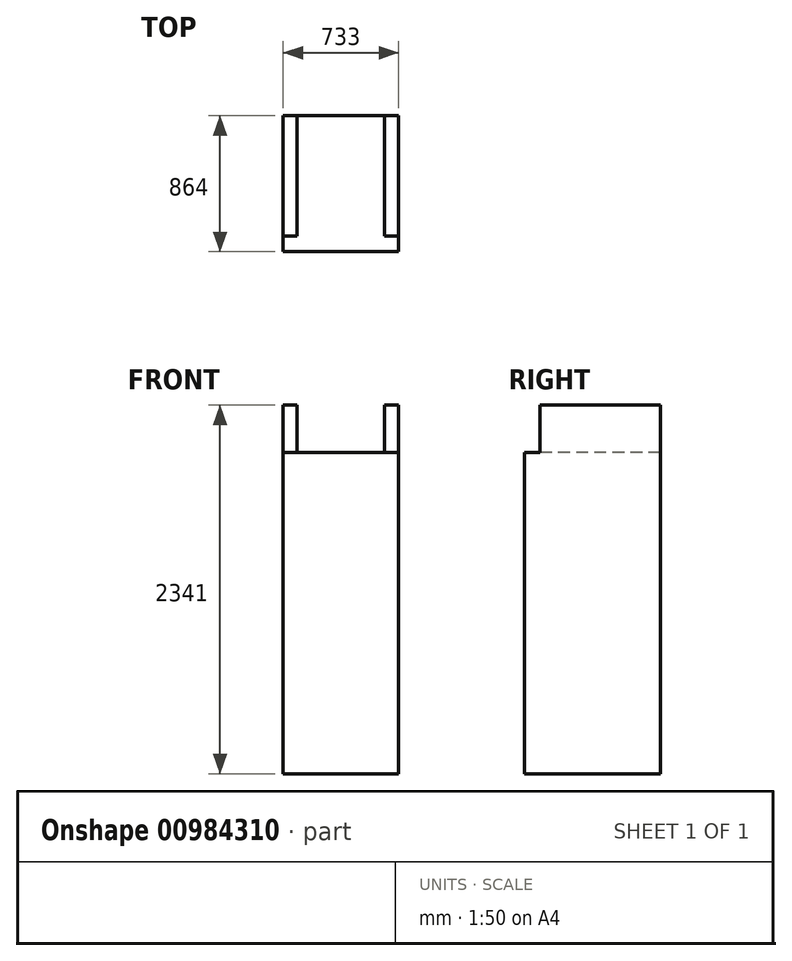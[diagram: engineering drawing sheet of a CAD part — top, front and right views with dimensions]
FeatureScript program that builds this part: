
annotation { "Feature Type Name" : "Feature", "Feature Type Description" : "" }
export const myFeature = defineFeature(function(context is Context, id is Id, definition is map)
    precondition{}
    {
        {
            var Q0;
            Q0=qCreatedBy(makeId("Top.planeOp"),FACE);
            var sketch = newSketch(context, id + "F0", { "sketchPlane" : qUnion([Q0])});
            skLineSegment(sketch, "E0.bottom", {"start": v(-733, 0) * mm, "end": v(0, 0) * mm});
            skLineSegment(sketch, "E0.top", {"start": v(-733, -764) * mm, "end": v(0, -764) * mm});
            skLineSegment(sketch, "E0.left", {"start": v(-733, 0) * mm, "end": v(-733, -764) * mm});
            skLineSegment(sketch, "E0.right", {"start": v(0, 0) * mm, "end": v(0, -764) * mm});
            skSolve(sketch);
        }
        {
            var Q0;
            Q0=makeQuery(id+"F0.imprint","IMPRINT",FACE,{"disambiguationData":[TD([[makeQuery(id+"F0.imprint","IMPRINT",EDGE,{"derivedFrom":sQuery(id+"F0.wireOp",EDGE,"E0.bottom")}),-1.0]])]});
            extrude(context, id + "F1", {"entities" : qUnion([Q0]), "depth" : 2341 * mm, "offsetDistance" : 25 * mm});
        }
        {
            var Q0;
            Q0=makeQuery(id+"F1.opExtrude","SWEPT_FACE",FACE,{"disambiguationData":[OSD([sQuery(id+"F0.wireOp",EDGE,"E0.top")])]});
            var sketch = newSketch(context, id + "F2", { "sketchPlane" : qUnion([Q0])});
            skLineSegment(sketch, "E1.bottom", {"start": v(-644.5, 2341) * mm, "end": v(-88.5, 2341) * mm});
            skLineSegment(sketch, "E1.top", {"start": v(-644.5, 2040) * mm, "end": v(-88.5, 2040) * mm});
            skLineSegment(sketch, "E1.left", {"start": v(-644.5, 2341) * mm, "end": v(-644.5, 2040) * mm});
            skLineSegment(sketch, "E1.right", {"start": v(-88.5, 2341) * mm, "end": v(-88.5, 2040) * mm});
            skLineSegment(sketch, "E2", {"start": v(-366.5, 2341) * mm, "end": v(-366.5, 2040) * mm, "construction": true});
            skSolve(sketch);
        }
        {
            var Q0;
            Q0=makeQuery(id+"F2.imprint","IMPRINT",FACE,{"disambiguationData":[TD([[makeQuery(id+"F2.imprint","IMPRINT",EDGE,{"derivedFrom":sQuery(id+"F2.wireOp",EDGE,"E1.bottom")}),-1.0]])]});
            extrude(context, id + "F3", {"entities" : qUnion([Q0]), "operationType" : NewBodyOperationType.REMOVE, "endBound" : BoundingType.THROUGH_ALL, "oppositeDirection" : true, "depth" : 25 * mm, "offsetDistance" : 25 * mm});
        }
        {
            var Q0;
            Q0=makeQuery(id+"F1.opExtrude","SWEPT_FACE",FACE,{"disambiguationData":[OSD([sQuery(id+"F0.wireOp",EDGE,"E0.top")])]});
            var sketch = newSketch(context, id + "F4", { "sketchPlane" : qUnion([Q0])});
            skLineSegment(sketch, "E3.bottom", {"start": v(-733, 0) * mm, "end": v(0, 0) * mm});
            skLineSegment(sketch, "E3.top", {"start": v(-733, 2040) * mm, "end": v(0, 2040) * mm});
            skLineSegment(sketch, "E3.left", {"start": v(-733, 0) * mm, "end": v(-733, 2040) * mm});
            skLineSegment(sketch, "E3.right", {"start": v(0, 0) * mm, "end": v(0, 2040) * mm});
            skSolve(sketch);
        }
        {
            var Q0;
            Q0=makeQuery(id+"F4.imprint","IMPRINT",FACE,{"disambiguationData":[TD([[makeQuery(id+"F4.imprint","IMPRINT",EDGE,{"derivedFrom":sQuery(id+"F4.wireOp",EDGE,"E3.bottom")}),1.0]])]});
            extrude(context, id + "F5", {"entities" : qUnion([Q0]), "operationType" : NewBodyOperationType.ADD, "depth" : 100 * mm, "offsetDistance" : 25 * mm});
        }
    });
